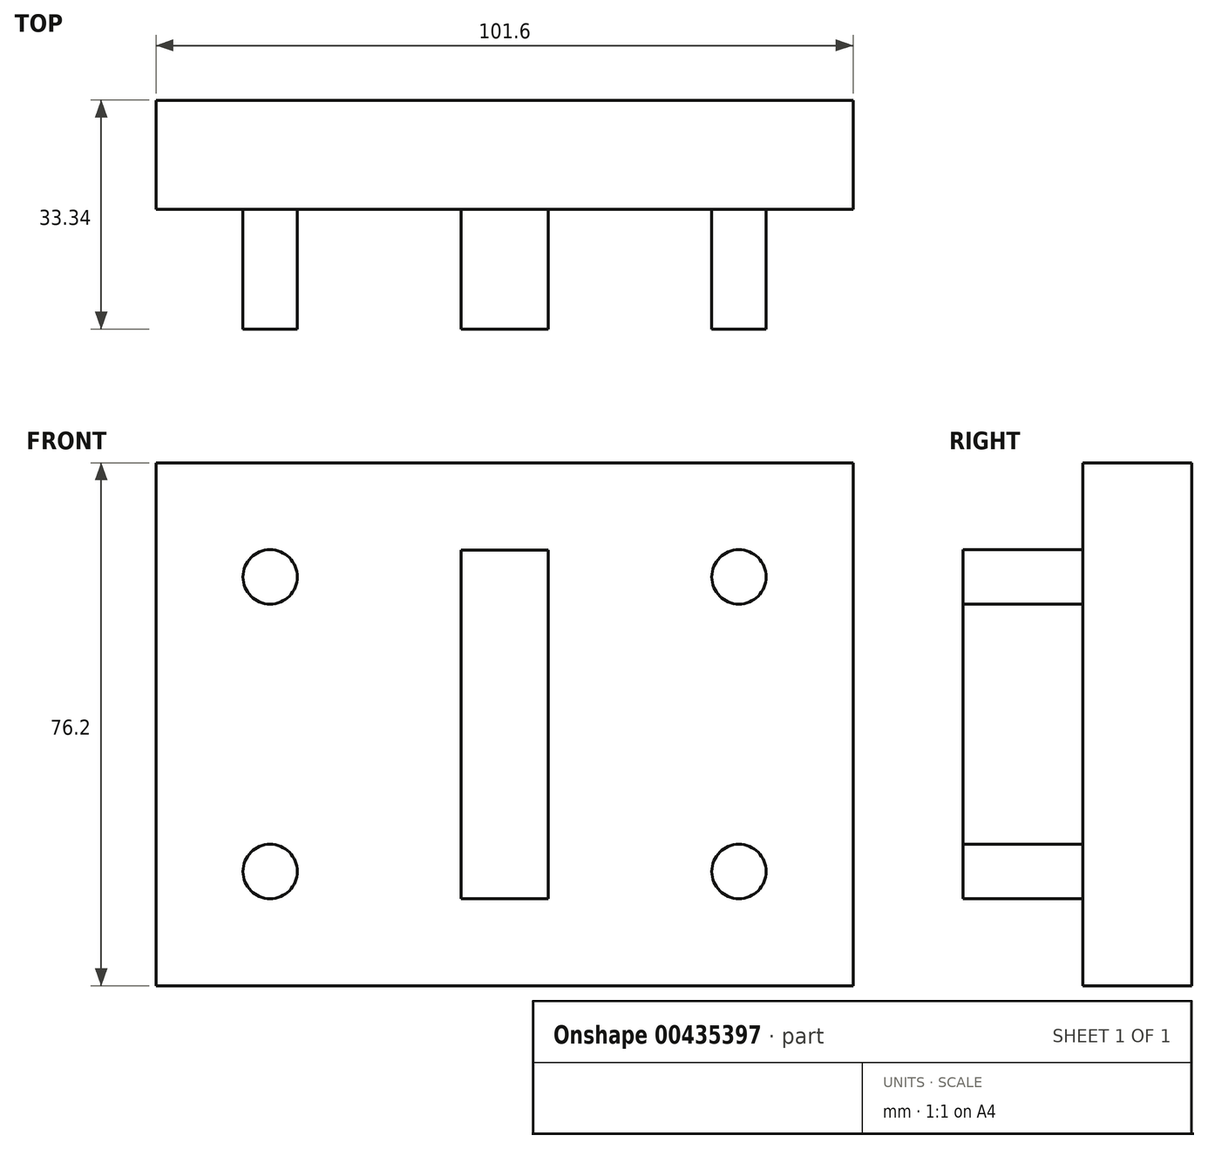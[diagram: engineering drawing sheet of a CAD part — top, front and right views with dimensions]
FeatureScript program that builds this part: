
annotation { "Feature Type Name" : "Feature", "Feature Type Description" : "" }
export const myFeature = defineFeature(function(context is Context, id is Id, definition is map)
    precondition{}
    {
        {
            var Q0;
            Q0=qCreatedBy(makeId("Front.planeOp"),FACE);
            var sketch = newSketch(context, id + "F0", { "sketchPlane" : qUnion([Q0])});
            skLineSegment(sketch, "E0.bottom", {"start": v(50.8, 38.1) * mm, "end": v(-50.8, 38.1) * mm});
            skLineSegment(sketch, "E0.top", {"start": v(50.8, -38.1) * mm, "end": v(-50.8, -38.1) * mm});
            skLineSegment(sketch, "E0.left", {"start": v(50.8, 38.1) * mm, "end": v(50.8, -38.1) * mm});
            skLineSegment(sketch, "E0.right", {"start": v(-50.8, 38.1) * mm, "end": v(-50.8, -38.1) * mm});
            skPoint(sketch, "E0.middle", {"position": v(0, 0) * mm});
            skSolve(sketch);
        }
        {
            var Q0;
            Q0=makeQuery(id+"F0.imprint","IMPRINT",FACE,{"disambiguationData":[TD([[makeQuery(id+"F0.imprint","IMPRINT",EDGE,{"derivedFrom":sQuery(id+"F0.wireOp",EDGE,"E0.bottom")}),1.0]])]});
            extrude(context, id + "F1", {"entities" : qUnion([Q0]), "endBound" : BoundingType.SYMMETRIC, "depth" : 15.88 * mm});
        }
        {
            var Q0;
            Q0=qCreatedBy(makeId("Front.planeOp"),FACE);
            var sketch = newSketch(context, id + "F2", { "sketchPlane" : qUnion([Q0])});
            skCircle(sketch, "E1", {"center": v(34.16, 21.46) * mm, "radius": 3.96 * mm});
            skCircle(sketch, "E2", {"center": v(34.16, -21.46) * mm, "radius": 3.96 * mm});
            skLineSegment(sketch, "E3.bottom", {"start": v(6.35, 25.4) * mm, "end": v(-6.35, 25.4) * mm});
            skLineSegment(sketch, "E3.top", {"start": v(6.35, -25.4) * mm, "end": v(-6.35, -25.4) * mm});
            skLineSegment(sketch, "E3.left", {"start": v(6.35, 25.4) * mm, "end": v(6.35, -25.4) * mm});
            skLineSegment(sketch, "E3.right", {"start": v(-6.35, 25.4) * mm, "end": v(-6.35, -25.4) * mm});
            skPoint(sketch, "E3.middle", {"position": v(0, 0) * mm});
            skCircle(sketch, "E4.MirrorC", {"center": v(-34.16, 21.46) * mm, "radius": 3.96 * mm});
            skCircle(sketch, "E5.MirrorC", {"center": v(-34.16, -21.46) * mm, "radius": 3.96 * mm});
            skSolve(sketch);
        }
        {
            var Q0;
            Q0 = qSketchRegion(id + "F2", true);
            extrude(context, id + "F3", {"entities" : qUnion([Q0]), "operationType" : NewBodyOperationType.ADD, "depth" : 25.4 * mm});
        }
    });
